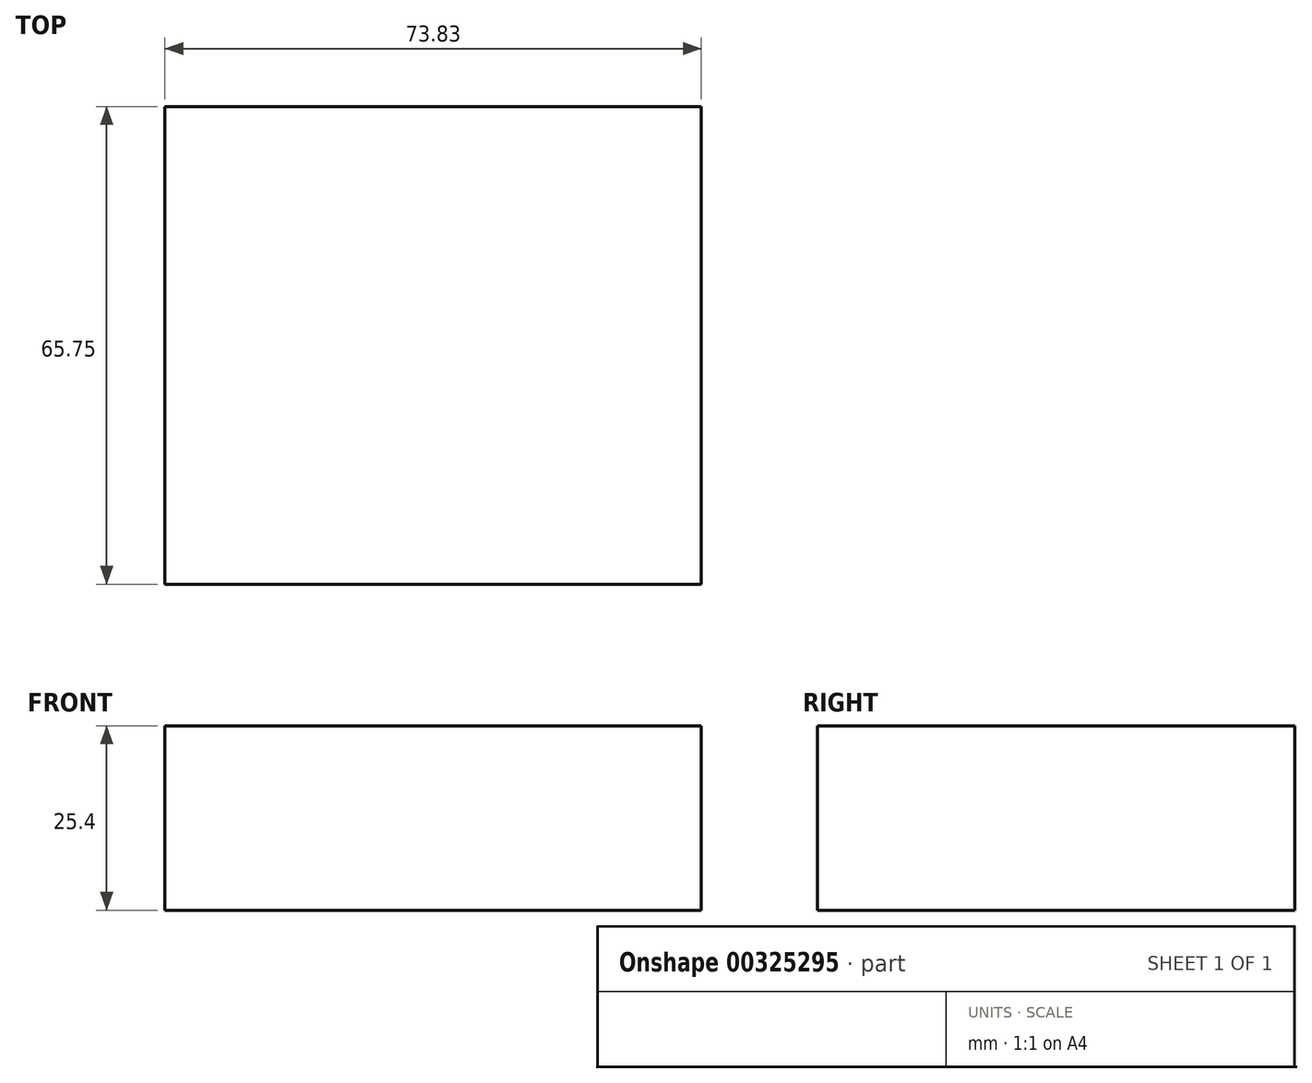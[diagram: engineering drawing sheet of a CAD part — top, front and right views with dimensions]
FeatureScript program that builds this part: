
annotation { "Feature Type Name" : "Feature", "Feature Type Description" : "" }
export const myFeature = defineFeature(function(context is Context, id is Id, definition is map)
    precondition{}
    {
        {
            var Q0;
            Q0=qCreatedBy(makeId("Top.planeOp"),FACE);
            var sketch = newSketch(context, id + "F0", { "sketchPlane" : qUnion([Q0])});
            skLineSegment(sketch, "E0.bottom", {"start": v(-35.21, 41.18) * mm, "end": v(38.62, 41.18) * mm});
            skLineSegment(sketch, "E0.top", {"start": v(-35.21, -44.24) * mm, "end": v(38.62, -44.24) * mm});
            skLineSegment(sketch, "E0.left", {"start": v(-35.21, 41.18) * mm, "end": v(-35.21, -44.24) * mm});
            skLineSegment(sketch, "E0.right", {"start": v(38.62, 41.18) * mm, "end": v(38.62, -44.24) * mm});
            skSolve(sketch);
        }
        {
            var Q0;
            Q0=sQuery(id+"F0.wireOp",EDGE,"E0.top");
            extrude(context, id + "F1", {"bodyType" : ToolBodyType.SURFACE, "surfaceEntities" : qUnion([Q0]), "endBound" : BoundingType.SYMMETRIC, "depth" : 25.4 * mm});
        }
        {
            var Q0;
            Q0=makeQuery(id+"F1.opExtrude","SWEPT_FACE",FACE,{"disambiguationData":[OSD([sQuery(id+"F0.wireOp",EDGE,"E0.top")])]});
            extrude(context, id + "F2", {"entities" : qUnion([Q0]), "oppositeDirection" : true, "depth" : 65.75 * mm});
        }
    });
